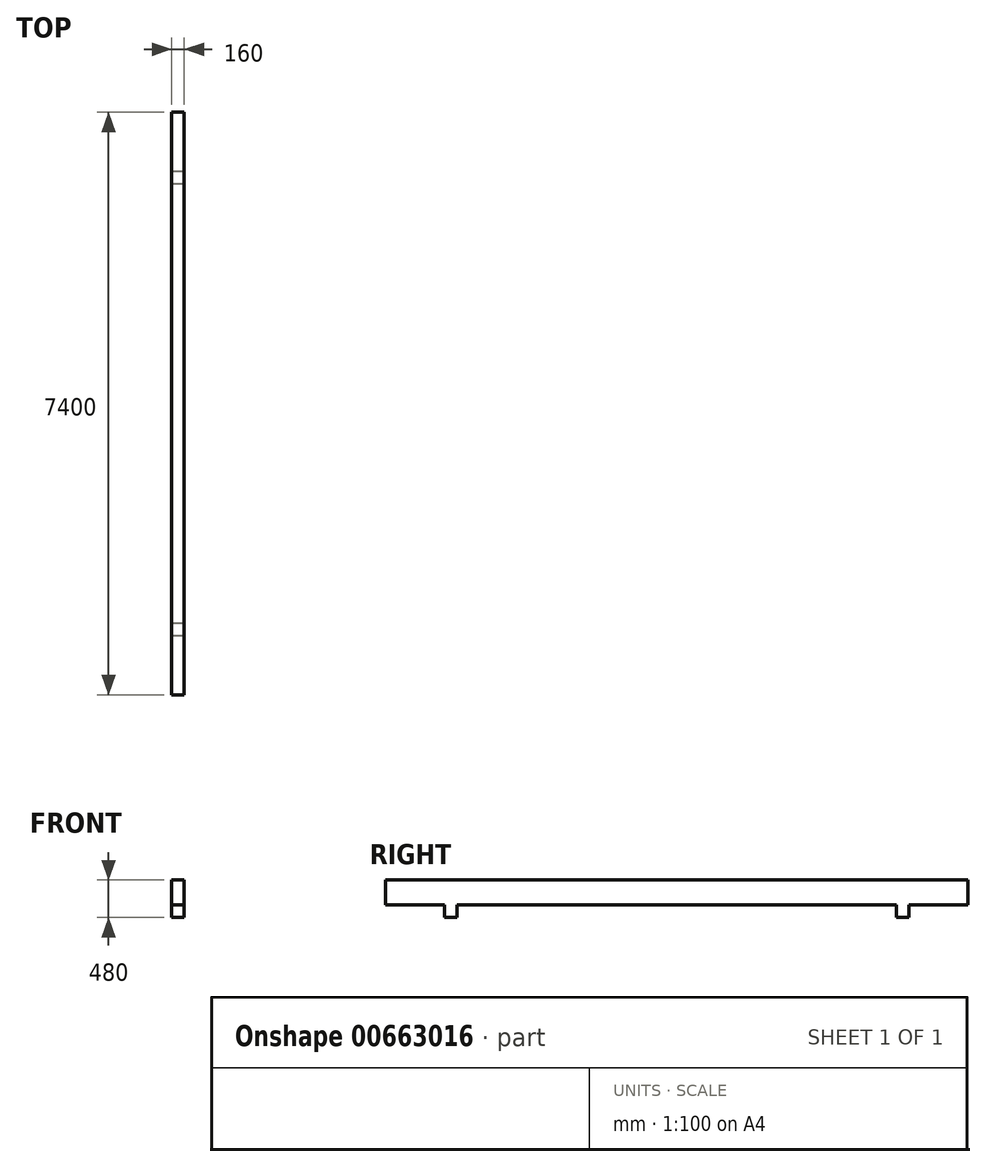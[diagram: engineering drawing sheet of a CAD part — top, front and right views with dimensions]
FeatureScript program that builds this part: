
annotation { "Feature Type Name" : "Feature", "Feature Type Description" : "" }
export const myFeature = defineFeature(function(context is Context, id is Id, definition is map)
    precondition{}
    {
        {
            var Q0;
            Q0=qCreatedBy(makeId("Front.planeOp"),FACE);
            var sketch = newSketch(context, id + "F0", { "sketchPlane" : qUnion([Q0])});
            skLineSegment(sketch, "E0.bottom", {"start": v(0, 0) * mm, "end": v(160, 0) * mm});
            skLineSegment(sketch, "E0.top", {"start": v(0, -320) * mm, "end": v(160, -320) * mm});
            skLineSegment(sketch, "E0.left", {"start": v(0, 0) * mm, "end": v(0, -320) * mm});
            skLineSegment(sketch, "E0.right", {"start": v(160, 0) * mm, "end": v(160, -320) * mm});
            skSolve(sketch);
        }
        {
            var Q0;
            Q0=makeQuery(id+"F0.imprint","IMPRINT",FACE,{"disambiguationData":[TD([[makeQuery(id+"F0.imprint","IMPRINT",EDGE,{"derivedFrom":sQuery(id+"F0.wireOp",EDGE,"E0.bottom")}),-1.0]])]});
            extrude(context, id + "F1", {"entities" : qUnion([Q0]), "depth" : 7400 * mm, "offsetDistance" : 25 * mm});
        }
        {
            var Q0;
            Q0=makeQuery(id+"F1.opExtrude","SWEPT_FACE",FACE,{"disambiguationData":[OSD([sQuery(id+"F0.wireOp",EDGE,"E0.top")])]});
            var sketch = newSketch(context, id + "F2", { "sketchPlane" : qUnion([Q0])});
            skLineSegment(sketch, "E1.bottom", {"start": v(160, 6650) * mm, "end": v(0, 6650) * mm});
            skLineSegment(sketch, "E1.top", {"start": v(160, 6490) * mm, "end": v(0, 6490) * mm});
            skLineSegment(sketch, "E1.left", {"start": v(160, 6650) * mm, "end": v(160, 6490) * mm});
            skLineSegment(sketch, "E1.right", {"start": v(0, 6650) * mm, "end": v(0, 6490) * mm});
            skLineSegment(sketch, "E2.bottom", {"start": v(160, 750) * mm, "end": v(0, 750) * mm});
            skLineSegment(sketch, "E2.top", {"start": v(160, 910) * mm, "end": v(0, 910) * mm});
            skLineSegment(sketch, "E2.left", {"start": v(160, 750) * mm, "end": v(160, 910) * mm});
            skLineSegment(sketch, "E2.right", {"start": v(0, 750) * mm, "end": v(0, 910) * mm});
            skSolve(sketch);
        }
        {
            var Q0;
            Q0=makeQuery(id+"F2.imprint","IMPRINT",FACE,{"disambiguationData":[TD([[makeQuery(id+"F2.imprint","IMPRINT",EDGE,{"derivedFrom":sQuery(id+"F2.wireOp",EDGE,"E1.bottom")}),1.0]])]});
            var Q1;
            Q1=makeQuery(id+"F2.imprint","IMPRINT",FACE,{"disambiguationData":[TD([[makeQuery(id+"F2.imprint","IMPRINT",EDGE,{"derivedFrom":sQuery(id+"F2.wireOp",EDGE,"E2.bottom")}),-1.0]])]});
            extrude(context, id + "F3", {"entities" : qUnion([Q0, Q1]), "operationType" : NewBodyOperationType.ADD, "depth" : 160 * mm, "offsetDistance" : 25 * mm});
        }
    });
